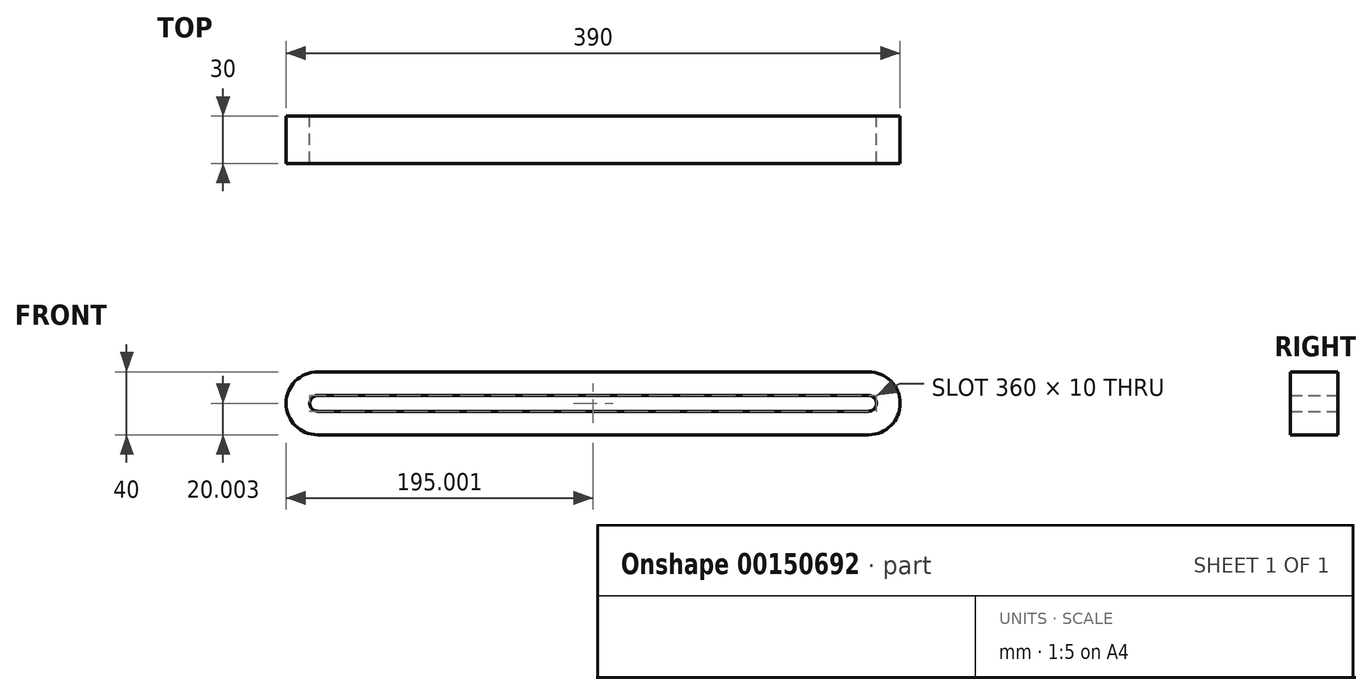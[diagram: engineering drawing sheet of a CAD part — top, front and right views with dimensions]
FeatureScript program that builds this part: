
annotation { "Feature Type Name" : "Feature", "Feature Type Description" : "" }
export const myFeature = defineFeature(function(context is Context, id is Id, definition is map)
    precondition{}
    {
        {
            var Q0;
            Q0=qCreatedBy(makeId("Front.planeOp"),FACE);
            var sketch = newSketch(context, id + "F0", { "sketchPlane" : qUnion([Q0])});
            skLineSegment(sketch, "E0.bottom", {"start": v(-257.43, -31.55) * mm, "end": v(92.57, -31.55) * mm});
            skLineSegment(sketch, "E0.top", {"start": v(-257.43, -41.55) * mm, "end": v(92.57, -41.55) * mm});
            skArc(sketch, "E1", {"start": v(-257.43, -31.55) * mm, "mid": v(-262.43, -36.55) * mm, "end": v(-257.43, -41.55) * mm});
            skArc(sketch, "E2", {"start": v(92.57, -41.55) * mm, "mid": v(97.57, -36.55) * mm, "end": v(92.57, -31.55) * mm});
            skLineSegment(sketch, "E3.bottom", {"start": v(-257.43, -16.55) * mm, "end": v(92.57, -16.55) * mm});
            skLineSegment(sketch, "E3.top", {"start": v(-257.43, -56.55) * mm, "end": v(92.57, -56.55) * mm});
            skArc(sketch, "E4", {"start": v(92.57, -56.55) * mm, "mid": v(112.57, -36.55) * mm, "end": v(92.57, -16.55) * mm});
            skArc(sketch, "E5", {"start": v(-257.43, -16.55) * mm, "mid": v(-277.43, -36.55) * mm, "end": v(-257.43, -56.55) * mm});
            skSolve(sketch);
        }
        {
            var Q0;
            Q0=makeQuery(id+"F0.imprint","IMPRINT",FACE,{"disambiguationData":[TD([[makeQuery(id+"F0.imprint","IMPRINT",EDGE,{"derivedFrom":sQuery(id+"F0.wireOp",EDGE,"E0.bottom")}),1.0]])]});
            extrude(context, id + "F1", {"entities" : qUnion([Q0]), "depth" : 5 * mm});
        }
        {
            var Q0;
            Q0=makeQuery(id+"F1.opExtrude","CAP_FACE",FACE,{"disambiguationData":[OSD([sQuery(id+"F0.wireOp",EDGE,"E0.bottom"),sQuery(id+"F0.wireOp",EDGE,"E0.top"),sQuery(id+"F0.wireOp",EDGE,"E1"),sQuery(id+"F0.wireOp",EDGE,"E2"),sQuery(id+"F0.wireOp",EDGE,"E3.bottom"),sQuery(id+"F0.wireOp",EDGE,"E3.top"),sQuery(id+"F0.wireOp",EDGE,"E4"),sQuery(id+"F0.wireOp",EDGE,"E5")])],"isStart":false});
            extrude(context, id + "F2", {"entities" : qUnion([Q0]), "operationType" : NewBodyOperationType.ADD, "depth" : 25 * mm});
        }
    });
